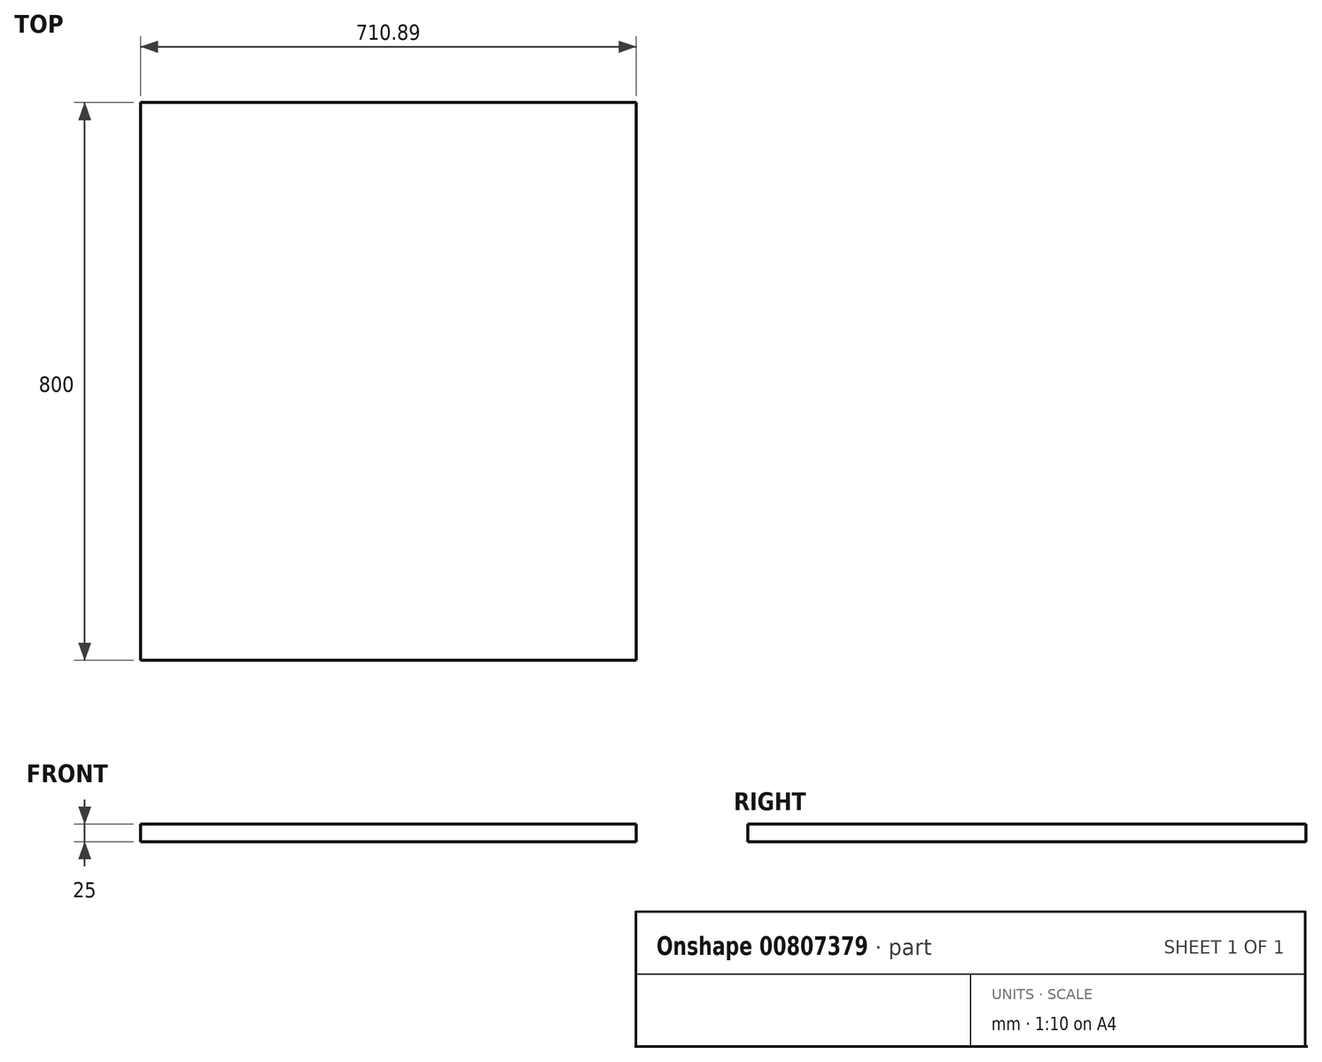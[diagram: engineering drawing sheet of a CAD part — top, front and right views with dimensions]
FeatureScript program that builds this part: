
annotation { "Feature Type Name" : "Feature", "Feature Type Description" : "" }
export const myFeature = defineFeature(function(context is Context, id is Id, definition is map)
    precondition{}
    {
        {
            var Q0;
            Q0=qCreatedBy(makeId("Top.planeOp"),FACE);
            var sketch = newSketch(context, id + "F0", { "sketchPlane" : qUnion([Q0])});
            skLineSegment(sketch, "E0.bottom", {"start": v(0, 0) * mm, "end": v(710.9, 0) * mm});
            skLineSegment(sketch, "E0.top", {"start": v(0, 800) * mm, "end": v(710.9, 800) * mm});
            skLineSegment(sketch, "E0.left", {"start": v(0, 0) * mm, "end": v(0, 800) * mm});
            skLineSegment(sketch, "E0.right", {"start": v(710.9, 0) * mm, "end": v(710.9, 800) * mm});
            skSolve(sketch);
        }
        {
            var Q0;
            Q0 = qSketchRegion(id + "F0", true);
            extrude(context, id + "F1", {"entities" : qUnion([Q0]), "depth" : 25 * mm, "offsetDistance" : 25 * mm});
        }
    });
